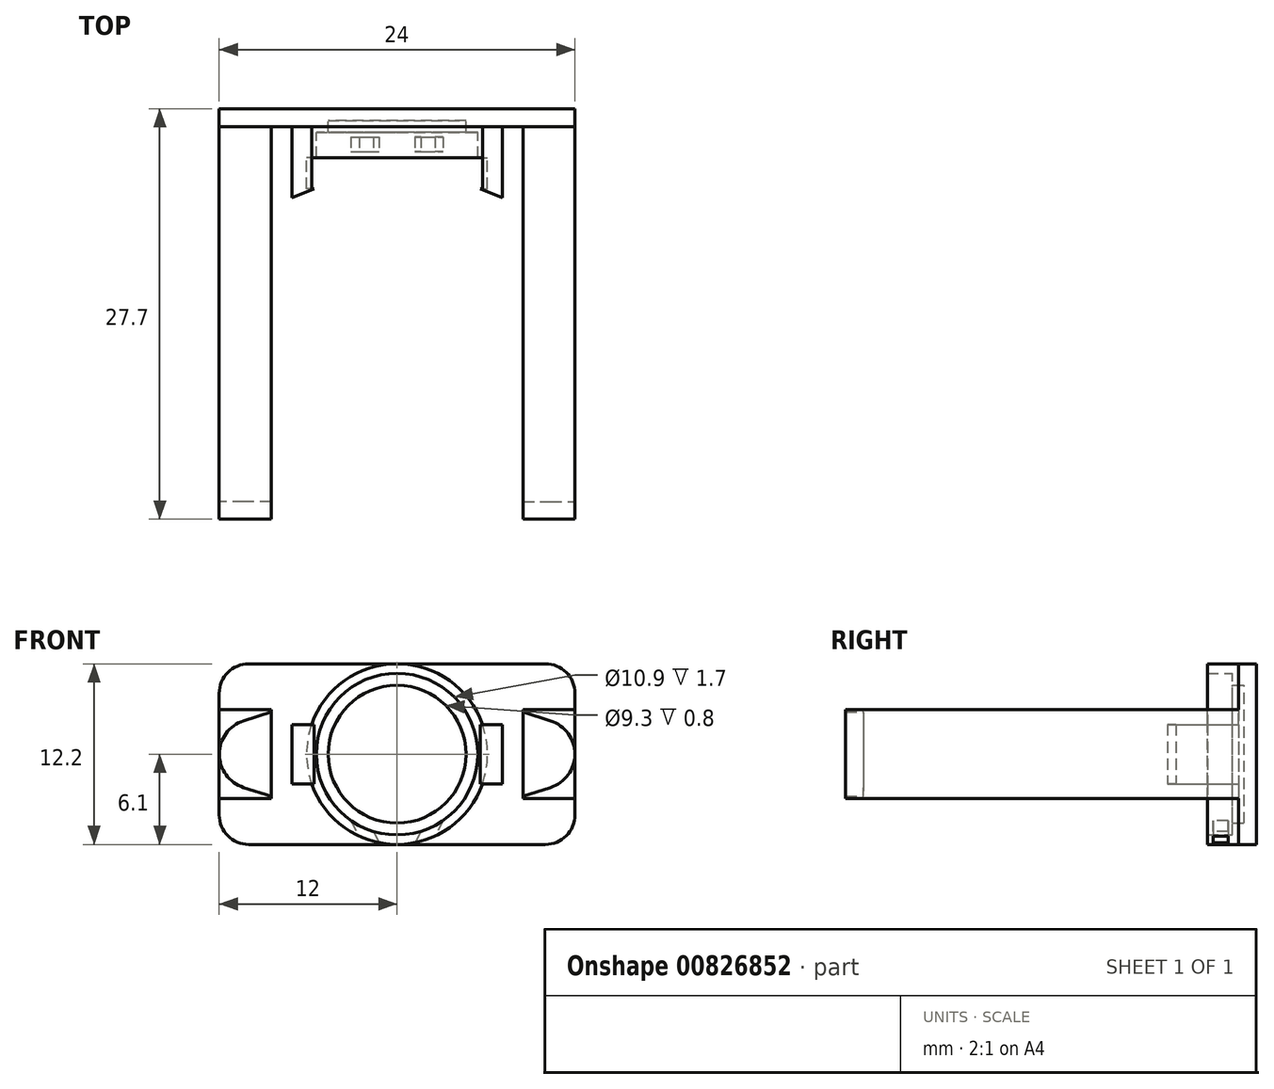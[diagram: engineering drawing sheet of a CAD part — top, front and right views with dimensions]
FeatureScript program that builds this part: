
annotation { "Feature Type Name" : "Feature", "Feature Type Description" : "" }
export const myFeature = defineFeature(function(context is Context, id is Id, definition is map)
    precondition{}
    {
        {
            var Q0;
            Q0=qCreatedBy(makeId("Front.planeOp"),FACE);
            var sketch = newSketch(context, id + "F0", { "sketchPlane" : qUnion([Q0])});
            skCircle(sketch, "E0", {"center": v(0, 0) * mm, "radius": 5 * mm});
            skCircle(sketch, "E1", {"center": v(0, 0) * mm, "radius": 6.1 * mm});
            skSolve(sketch);
        }
        {
            var Q0;
            Q0=makeQuery(id+"F0.imprint","IMPRINT",FACE,{"disambiguationData":[TD([[makeQuery(id+"F0.imprint","IMPRINT",EDGE,{"derivedFrom":sQuery(id+"F0.wireOp",EDGE,"E0")}),-1.0]])]});
            var Q1;
            Q1=makeQuery(id+"F0.imprint","IMPRINT",FACE,{"disambiguationData":[TD([[makeQuery(id+"F0.imprint","IMPRINT",EDGE,{"derivedFrom":sQuery(id+"F0.wireOp",EDGE,"E0")}),1.0]])]});
            extrude(context, id + "F1", {"entities" : qUnion([Q0, Q1]), "depth" : 0.8 * mm, "offsetDistance" : 25 * mm});
        }
        {
            var Q0;
            Q0=makeQuery(id+"F1.opExtrude","CAP_FACE",FACE,{"disambiguationData":[OSD([sQuery(id+"F0.wireOp",EDGE,"E1")])],"isStart":false});
            var sketch = newSketch(context, id + "F2", { "sketchPlane" : qUnion([Q0])});
            skCircle(sketch, "E2", {"center": v(0, 0) * mm, "radius": 5.45 * mm});
            skCircle(sketch, "E3", {"center": v(0, 0) * mm, "radius": 6.1 * mm});
            skSolve(sketch);
        }
        {
            var Q0;
            Q0=makeQuery(id+"F2.imprint","IMPRINT",FACE,{"disambiguationData":[TD([[makeQuery(id+"F2.imprint","IMPRINT",EDGE,{"derivedFrom":sQuery(id+"F2.wireOp",EDGE,"E2")}),-1.0]])]});
            extrude(context, id + "F3", {"entities" : qUnion([Q0]), "operationType" : NewBodyOperationType.ADD, "depth" : 2.5 * mm, "offsetDistance" : 25 * mm});
        }
        {
            var Q0;
            Q0=makeQuery(id+"F1.opExtrude","CAP_FACE",FACE,{"disambiguationData":[OSD([sQuery(id+"F0.wireOp",EDGE,"E1")])],"isStart":false});
            var sketch = newSketch(context, id + "F4", { "sketchPlane" : qUnion([Q0])});
            skCircle(sketch, "E4", {"center": v(0, 0) * mm, "radius": 4.65 * mm});
            skSolve(sketch);
        }
        {
            var Q0;
            Q0=makeQuery(id+"F4.imprint","IMPRINT",FACE,{"disambiguationData":[TD([[makeQuery(id+"F4.imprint","IMPRINT",EDGE,{"derivedFrom":sQuery(id+"F4.wireOp",EDGE,"E4")}),-1.0]])]});
            extrude(context, id + "F5", {"entities" : qUnion([Q0]), "operationType" : NewBodyOperationType.ADD, "depth" : 0.8 * mm, "offsetDistance" : 25 * mm});
        }
        {
            var Q0;
            Q0=makeQuery(id+"F3.opExtrude","CAP_FACE",FACE,{"disambiguationData":[OSD([sQuery(id+"F2.wireOp",EDGE,"E2"),sQuery(id+"F2.wireOp",EDGE,"E3")])],"isStart":false});
            var sketch = newSketch(context, id + "F6", { "sketchPlane" : qUnion([Q0])});
            skLineSegment(sketch, "E5", {"start": v(-1.6, -5.2) * mm, "end": v(-1.2, -5.98) * mm});
            skLineSegment(sketch, "E6", {"start": v(-3.1, -4.48) * mm, "end": v(-2.56, -5.54) * mm});
            skLineSegment(sketch, "E7.MirrorCS", {"start": v(1.6, -5.2) * mm, "end": v(1.2, -5.98) * mm});
            skLineSegment(sketch, "E8.MirrorCS", {"start": v(3.1, -4.48) * mm, "end": v(2.56, -5.54) * mm});
            skSolve(sketch);
        }
        {
            var Q0;
            {var subQ0=sQuery(id+"F6.wireOp",EDGE,"E5");Q0=makeQuery(id+"F6.imprint","IMPRINT",FACE,{"disambiguationData":[TD([[makeQuery(id+"F6.imprint","IMPRINT",EDGE,{"derivedFrom":subQ0}),-1.0]])]});}
            var Q1;
            {var subQ0=sQuery(id+"F6.wireOp",EDGE,"E7.MirrorCS");Q1=makeQuery(id+"F6.imprint","IMPRINT",FACE,{"disambiguationData":[TD([[makeQuery(id+"F6.imprint","IMPRINT",EDGE,{"derivedFrom":subQ0}),1.0]])]});}
            extrude(context, id + "F7", {"entities" : qUnion([Q0, Q1]), "operationType" : NewBodyOperationType.REMOVE, "oppositeDirection" : true, "depth" : 1.4 * mm, "offsetDistance" : 25 * mm});
        }
        {
            var Q0;
            {var subQ0=sQuery(id+"F2.wireOp",EDGE,"E3");var subQ1=sQuery(id+"F2.wireOp",EDGE,"E2");Q0=makeQuery(id+"F7.boolean.opBoolean","SPLIT",FACE,{"disambiguationData":[TD([makeQuery(id+"F7.opExtrude","SWEPT_FACE",FACE,{"disambiguationData":[OSD([sQuery(id+"F6.wireOp",EDGE,"E6")])]})])],"derivedFrom":makeQuery(id+"F3.opExtrude","CAP_FACE",FACE,{"disambiguationData":[OSD([subQ1,subQ0])],"isStart":false})});}
            var sketch = newSketch(context, id + "F8", { "sketchPlane" : qUnion([Q0])});
            skArc(sketch, "E9", {"start": v(-3.1, -4.48) * mm, "mid": v(-2.38, -4.9) * mm, "end": v(-1.6, -5.2) * mm});
            skArc(sketch, "E10", {"start": v(-2.56, -5.54) * mm, "mid": v(-1.9, -5.8) * mm, "end": v(-1.2, -5.98) * mm});
            skLineSegment(sketch, "E11", {"start": v(-3.1, -4.48) * mm, "end": v(-2.56, -5.54) * mm});
            skLineSegment(sketch, "E12", {"start": v(-1.6, -5.2) * mm, "end": v(-1.2, -5.98) * mm});
            skLineSegment(sketch, "E13.MirrorCS", {"start": v(3.1, -4.48) * mm, "end": v(2.56, -5.54) * mm});
            skArc(sketch, "E14.MirrorCS", {"start": v(2.56, -5.54) * mm, "mid": v(1.9, -5.8) * mm, "end": v(1.2, -5.98) * mm});
            skLineSegment(sketch, "E15.MirrorCS", {"start": v(1.6, -5.2) * mm, "end": v(1.2, -5.98) * mm});
            skArc(sketch, "E16.MirrorCS", {"start": v(3.1, -4.48) * mm, "mid": v(2.38, -4.9) * mm, "end": v(1.6, -5.2) * mm});
            skSolve(sketch);
        }
        {
            var Q0;
            Q0=makeQuery(id+"F8.imprint","IMPRINT",FACE,{"disambiguationData":[TD([[makeQuery(id+"F8.imprint","IMPRINT",EDGE,{"derivedFrom":sQuery(id+"F8.wireOp",EDGE,"E9")}),-1.0]])]});
            var Q1;
            Q1=makeQuery(id+"F8.imprint","IMPRINT",FACE,{"disambiguationData":[TD([[makeQuery(id+"F8.imprint","IMPRINT",EDGE,{"derivedFrom":sQuery(id+"F8.wireOp",EDGE,"E13.MirrorCS")}),-1.0]])]});
            extrude(context, id + "F9", {"entities" : qUnion([Q0, Q1]), "operationType" : NewBodyOperationType.ADD, "oppositeDirection" : true, "depth" : 0.4 * mm, "offsetDistance" : 25 * mm});
        }
        {
            var Q0;
            Q0=makeQuery(id+"F1.opExtrude","CAP_FACE",FACE,{"disambiguationData":[OSD([sQuery(id+"F0.wireOp",EDGE,"E1")])],"isStart":true});
            var sketch = newSketch(context, id + "F10", { "sketchPlane" : qUnion([Q0])});
            skLineSegment(sketch, "E17.bottom", {"start": v(-12, -6.1) * mm, "end": v(12, -6.1) * mm});
            skLineSegment(sketch, "E17.top", {"start": v(-12, 6.1) * mm, "end": v(12, 6.1) * mm});
            skLineSegment(sketch, "E17.left", {"start": v(-12, -6.1) * mm, "end": v(-12, 6.1) * mm});
            skLineSegment(sketch, "E17.right", {"start": v(12, -6.1) * mm, "end": v(12, 6.1) * mm});
            skPoint(sketch, "E17.middle", {"position": v(0, 0) * mm});
            skSolve(sketch);
        }
        {
            var Q0;
            {var subQ0=sQuery(id+"F10.wireOp",EDGE,"E17.right");Q0=makeQuery(id+"F10.imprint","IMPRINT",FACE,{"disambiguationData":[TD([[makeQuery(id+"F10.imprint","IMPRINT",EDGE,{"derivedFrom":subQ0}),1.0]])]});}
            var Q1;
            {var subQ0=sQuery(id+"F10.wireOp",EDGE,"E17.left");Q1=makeQuery(id+"F10.imprint","IMPRINT",FACE,{"disambiguationData":[TD([[makeQuery(id+"F10.imprint","IMPRINT",EDGE,{"derivedFrom":subQ0}),-1.0]])]});}
            extrude(context, id + "F11", {"entities" : qUnion([Q0, Q1]), "operationType" : NewBodyOperationType.ADD, "oppositeDirection" : true, "depth" : 1.2 * mm, "offsetDistance" : 25 * mm});
        }
        {
            var Q0;
            Q0=makeQuery(id+"F11.opExtrude","SWEPT_EDGE",EDGE,{"disambiguationData":[OSD([sQuery(id+"F10.wireOp",EDGE,"E17.bottom"),sQuery(id+"F10.wireOp",EDGE,"E17.right")])]});
            var Q1;
            Q1=makeQuery(id+"F11.opExtrude","SWEPT_EDGE",EDGE,{"disambiguationData":[OSD([sQuery(id+"F10.wireOp",EDGE,"E17.bottom"),sQuery(id+"F10.wireOp",EDGE,"E17.left")])]});
            var Q2;
            Q2=makeQuery(id+"F11.opExtrude","SWEPT_EDGE",EDGE,{"disambiguationData":[OSD([sQuery(id+"F10.wireOp",EDGE,"E17.top"),sQuery(id+"F10.wireOp",EDGE,"E17.left")])]});
            var Q3;
            Q3=makeQuery(id+"F11.opExtrude","SWEPT_EDGE",EDGE,{"disambiguationData":[OSD([sQuery(id+"F10.wireOp",EDGE,"E17.top"),sQuery(id+"F10.wireOp",EDGE,"E17.right")])]});
            fillet(context, id + "F12", {"entities" : qUnion([Q0, Q1, Q2, Q3]), "radius" : 2 * mm, "tangentPropagation" : true, "allowEdgeOverflow" : false});
        }
        {
            var Q0;
            Q0=makeQuery(id+"F11.opExtrude","CAP_FACE",FACE,{"disambiguationData":[OSD([sQuery(id+"F0.wireOp",EDGE,"E1"),sQuery(id+"F10.wireOp",EDGE,"E17.bottom"),sQuery(id+"F10.wireOp",EDGE,"E17.top"),sQuery(id+"F10.wireOp",EDGE,"E17.right")])],"isStart":false});
            var sketch = newSketch(context, id + "F13", { "sketchPlane" : qUnion([Q0])});
            skLineSegment(sketch, "E18", {"start": v(-12, 3) * mm, "end": v(-8.5, 3) * mm});
            skLineSegment(sketch, "E19", {"start": v(-8.5, 3) * mm, "end": v(-8.5, -3) * mm});
            skLineSegment(sketch, "E20", {"start": v(-8.5, -3) * mm, "end": v(-12, -3) * mm});
            skLineSegment(sketch, "E21", {"start": v(-7.1, 2) * mm, "end": v(-7.1, -2) * mm});
            skLineSegment(sketch, "E22", {"start": v(-7.1, -2) * mm, "end": v(-5.76, -2) * mm});
            skLineSegment(sketch, "E23", {"start": v(-7.1, 2) * mm, "end": v(-5.76, 2) * mm});
            skSolve(sketch);
        }
        {
            var Q0;
            {var subQ0=sQuery(id+"F13.wireOp",EDGE,"E18");Q0=makeQuery(id+"F13.imprint","IMPRINT",FACE,{"disambiguationData":[TD([[makeQuery(id+"F13.imprint","IMPRINT",EDGE,{"derivedFrom":subQ0}),-1.0]])]});}
            extrude(context, id + "F14", {"entities" : qUnion([Q0]), "operationType" : NewBodyOperationType.ADD, "depth" : 25.3 * mm, "offsetDistance" : 25 * mm});
        }
        {
            var Q0;
            Q0=makeQuery(id+"F11.opExtrude","CAP_FACE",FACE,{"disambiguationData":[OSD([sQuery(id+"F0.wireOp",EDGE,"E1"),sQuery(id+"F10.wireOp",EDGE,"E17.bottom"),sQuery(id+"F10.wireOp",EDGE,"E17.top"),sQuery(id+"F10.wireOp",EDGE,"E17.left")])],"isStart":false});
            var sketch = newSketch(context, id + "F15", { "sketchPlane" : qUnion([Q0])});
            skLineSegment(sketch, "E24", {"start": v(12, 3) * mm, "end": v(8.5, 3) * mm});
            skLineSegment(sketch, "E25", {"start": v(8.5, 3) * mm, "end": v(8.5, -3) * mm});
            skLineSegment(sketch, "E26", {"start": v(8.5, -3) * mm, "end": v(12, -3) * mm});
            skLineSegment(sketch, "E27", {"start": v(7.1, 2) * mm, "end": v(7.1, -2) * mm});
            skLineSegment(sketch, "E28", {"start": v(7.1, -2) * mm, "end": v(5.76, -2) * mm});
            skLineSegment(sketch, "E29", {"start": v(7.1, 2) * mm, "end": v(5.76, 2) * mm});
            skSolve(sketch);
        }
        {
            var Q0;
            {var subQ0=sQuery(id+"F15.wireOp",EDGE,"E24");Q0=makeQuery(id+"F15.imprint","IMPRINT",FACE,{"disambiguationData":[TD([[makeQuery(id+"F15.imprint","IMPRINT",EDGE,{"derivedFrom":subQ0}),1.0]])]});}
            extrude(context, id + "F16", {"entities" : qUnion([Q0]), "operationType" : NewBodyOperationType.ADD, "depth" : 25.3 * mm, "offsetDistance" : 25 * mm});
        }
        {
            var Q0;
            Q0=makeQuery(id+"F15.imprint","IMPRINT",FACE,{"disambiguationData":[TD([[makeQuery(id+"F15.imprint","IMPRINT",EDGE,{"derivedFrom":sQuery(id+"F15.wireOp",EDGE,"E27")}),-1.0]])]});
            var Q1;
            Q1=makeQuery(id+"F13.imprint","IMPRINT",FACE,{"disambiguationData":[TD([[makeQuery(id+"F13.imprint","IMPRINT",EDGE,{"derivedFrom":sQuery(id+"F13.wireOp",EDGE,"E21")}),1.0]])]});
            extrude(context, id + "F17", {"entities" : qUnion([Q0, Q1]), "operationType" : NewBodyOperationType.ADD, "depth" : 4.2 * mm, "offsetDistance" : 25 * mm});
        }
        {
            var Q0;
            Q0=makeQuery(id+"F17.opExtrude","SWEPT_FACE",FACE,{"disambiguationData":[OSD([sQuery(id+"F13.wireOp",EDGE,"E22")])]});
            var sketch = newSketch(context, id + "F18", { "sketchPlane" : qUnion([Q0])});
            skLineSegment(sketch, "E30", {"start": v(-7.1, 5.4) * mm, "end": v(-7.1, 6) * mm});
            skLineSegment(sketch, "E31", {"start": v(-5.76, 5.4) * mm, "end": v(-5.66, 5.4) * mm});
            skLineSegment(sketch, "E32", {"start": v(-5.66, 5.4) * mm, "end": v(-7.1, 6) * mm});
            skSolve(sketch);
        }
        {
            var Q0;
            Q0=makeQuery(id+"F18.imprint","IMPRINT",FACE,{"disambiguationData":[TD([[makeQuery(id+"F18.imprint","IMPRINT",EDGE,{"derivedFrom":sQuery(id+"F18.wireOp",EDGE,"E30")}),-1.0]])]});
            extrude(context, id + "F19", {"entities" : qUnion([Q0]), "operationType" : NewBodyOperationType.ADD, "oppositeDirection" : true, "depth" : 4 * mm, "offsetDistance" : 25 * mm});
        }
        {
            var Q0;
            Q0=makeQuery(id+"F17.opExtrude","SWEPT_FACE",FACE,{"disambiguationData":[OSD([sQuery(id+"F15.wireOp",EDGE,"E28")])]});
            var sketch = newSketch(context, id + "F20", { "sketchPlane" : qUnion([Q0])});
            skLineSegment(sketch, "E33", {"start": v(7.1, 5.4) * mm, "end": v(7.1, 6) * mm});
            skLineSegment(sketch, "E34", {"start": v(5.76, 5.4) * mm, "end": v(5.66, 5.4) * mm});
            skLineSegment(sketch, "E35", {"start": v(5.66, 5.4) * mm, "end": v(7.1, 6) * mm});
            skSolve(sketch);
        }
        {
            var Q0;
            Q0=makeQuery(id+"F20.imprint","IMPRINT",FACE,{"disambiguationData":[TD([[makeQuery(id+"F20.imprint","IMPRINT",EDGE,{"derivedFrom":sQuery(id+"F20.wireOp",EDGE,"E33")}),1.0]])]});
            extrude(context, id + "F21", {"entities" : qUnion([Q0]), "operationType" : NewBodyOperationType.ADD, "oppositeDirection" : true, "depth" : 4 * mm, "offsetDistance" : 25 * mm});
        }
        {
            var Q0;
            {var subQ0=sQuery(id+"F13.wireOp",EDGE,"E22");Q0=makeQuery(id+"F19.boolean.opBoolean","MERGE",FACE,{"derivedFrom":[makeQuery(id+"F17.opExtrude","SWEPT_FACE",FACE,{"disambiguationData":[OSD([subQ0])]}),makeQuery(id+"F19.opExtrude","CAP_FACE",FACE,{"disambiguationData":[OSD([subQ0,sQuery(id+"F18.wireOp",EDGE,"E30"),sQuery(id+"F18.wireOp",EDGE,"scbSYdZa-IKE8-HjIA-PmpS-5iz6sRiiHXsu")])],"isStart":true})]});}
            var sketch = newSketch(context, id + "F22", { "sketchPlane" : qUnion([Q0])});
            skLineSegment(sketch, "E36", {"start": v(-5.76, 5.4) * mm, "end": v(-5.61, 5.4) * mm});
            skLineSegment(sketch, "E37", {"start": v(-5.61, 5.4) * mm, "end": v(-7.1, 6) * mm});
            skSolve(sketch);
        }
        {
            var Q0;
            Q0=makeQuery(id+"F22.imprint","IMPRINT",FACE,{"disambiguationData":[TD([[makeQuery(id+"F22.imprint","IMPRINT",EDGE,{"derivedFrom":sQuery(id+"F22.wireOp",EDGE,"E36")}),1.0]])]});
            extrude(context, id + "F23", {"entities" : qUnion([Q0]), "operationType" : NewBodyOperationType.ADD, "oppositeDirection" : true, "depth" : 4 * mm, "offsetDistance" : 25 * mm});
        }
        {
            var Q0;
            {var subQ0=sQuery(id+"F15.wireOp",EDGE,"E28");Q0=makeQuery(id+"F21.boolean.opBoolean","MERGE",FACE,{"derivedFrom":[makeQuery(id+"F17.opExtrude","SWEPT_FACE",FACE,{"disambiguationData":[OSD([subQ0])]}),makeQuery(id+"F21.opExtrude","CAP_FACE",FACE,{"disambiguationData":[OSD([subQ0,sQuery(id+"F20.wireOp",EDGE,"E33"),sQuery(id+"F20.wireOp",EDGE,"OUZQXp2e-nWsZ-sgYy-KXVV-Yu3MqT17kAb9")])],"isStart":true})]});}
            var sketch = newSketch(context, id + "F24", { "sketchPlane" : qUnion([Q0])});
            skLineSegment(sketch, "E38", {"start": v(5.76, 5.4) * mm, "end": v(5.61, 5.4) * mm});
            skLineSegment(sketch, "E39", {"start": v(5.61, 5.4) * mm, "end": v(7.1, 6) * mm});
            skSolve(sketch);
        }
        {
            var Q0;
            Q0=makeQuery(id+"F24.imprint","IMPRINT",FACE,{"disambiguationData":[TD([[makeQuery(id+"F24.imprint","IMPRINT",EDGE,{"derivedFrom":sQuery(id+"F24.wireOp",EDGE,"E38")}),-1.0]])]});
            extrude(context, id + "F25", {"entities" : qUnion([Q0]), "operationType" : NewBodyOperationType.ADD, "oppositeDirection" : true, "depth" : 4 * mm, "offsetDistance" : 25 * mm});
        }
        {
            var Q0;
            Q0=makeQuery(id+"F16.opExtrude","CAP_FACE",FACE,{"disambiguationData":[OSD([sQuery(id+"F10.wireOp",EDGE,"E17.left"),sQuery(id+"F15.wireOp",EDGE,"E24"),sQuery(id+"F15.wireOp",EDGE,"E25"),sQuery(id+"F15.wireOp",EDGE,"E26")])],"isStart":false});
            var sketch = newSketch(context, id + "F26", { "sketchPlane" : qUnion([Q0])});
            skLineSegment(sketch, "E40", {"start": v(8.5, 2.85) * mm, "end": v(10.35, 2.25) * mm});
            skArc(sketch, "E41", {"start": v(10.35, -2.25) * mm, "mid": v(11.99, 0) * mm, "end": v(10.35, 2.25) * mm});
            skLineSegment(sketch, "E42.MirrorCS", {"start": v(8.5, -2.85) * mm, "end": v(10.35, -2.25) * mm});
            skSolve(sketch);
        }
        {
            var Q0;
            {var subQ2=sQuery(id+"F26.wireOp",EDGE,"E40");Q0=makeQuery(id+"F26.imprint","IMPRINT",FACE,{"disambiguationData":[TD([[makeQuery(id+"F26.imprint","IMPRINT",EDGE,{"derivedFrom":subQ2}),1.0]])]});}
            extrude(context, id + "F27", {"entities" : qUnion([Q0]), "operationType" : NewBodyOperationType.ADD, "depth" : 1.2 * mm, "offsetDistance" : 25 * mm});
        }
        {
            var Q0;
            Q0=makeQuery(id+"F14.opExtrude","CAP_FACE",FACE,{"disambiguationData":[OSD([sQuery(id+"F10.wireOp",EDGE,"E17.right"),sQuery(id+"F13.wireOp",EDGE,"E18"),sQuery(id+"F13.wireOp",EDGE,"E19"),sQuery(id+"F13.wireOp",EDGE,"E20")])],"isStart":false});
            var sketch = newSketch(context, id + "F28", { "sketchPlane" : qUnion([Q0])});
            skLineSegment(sketch, "E43", {"start": v(-8.5, 2.85) * mm, "end": v(-10.35, 2.25) * mm});
            skLineSegment(sketch, "E44.MirrorCS", {"start": v(-8.5, -2.85) * mm, "end": v(-10.35, -2.25) * mm});
            skArc(sketch, "E45", {"start": v(-10.35, 2.25) * mm, "mid": v(-12, 0) * mm, "end": v(-10.35, -2.25) * mm});
            skSolve(sketch);
        }
        {
            var Q0;
            {var subQ2=sQuery(id+"F28.wireOp",EDGE,"E43");Q0=makeQuery(id+"F28.imprint","IMPRINT",FACE,{"disambiguationData":[TD([[makeQuery(id+"F28.imprint","IMPRINT",EDGE,{"derivedFrom":subQ2}),-1.0]])]});}
            extrude(context, id + "F29", {"entities" : qUnion([Q0]), "operationType" : NewBodyOperationType.ADD, "depth" : 1.2 * mm, "offsetDistance" : 25 * mm});
        }
    });
